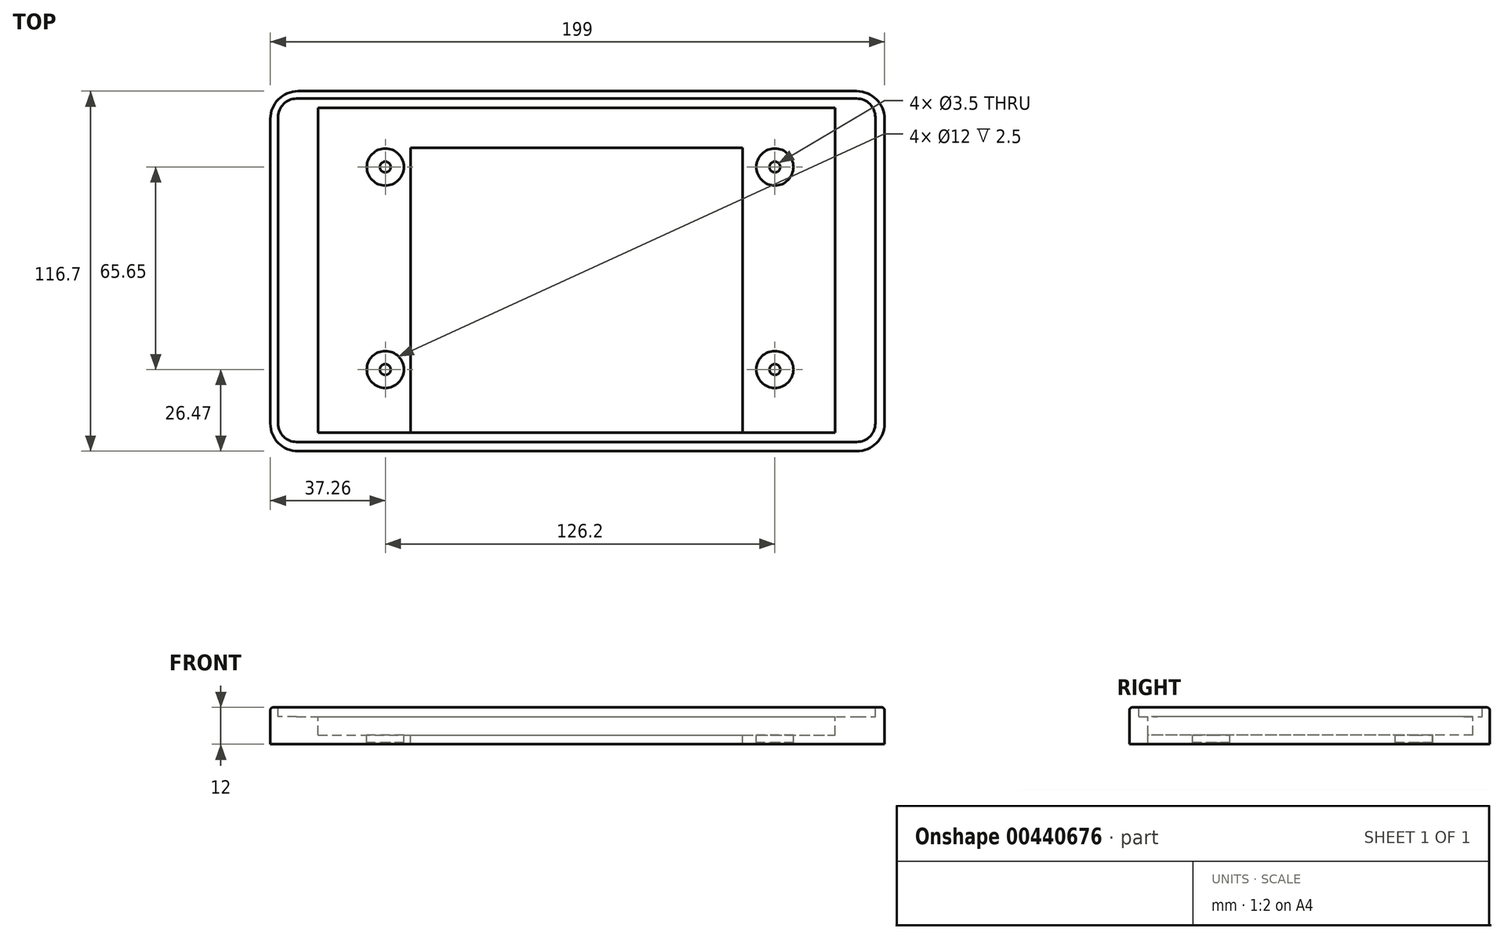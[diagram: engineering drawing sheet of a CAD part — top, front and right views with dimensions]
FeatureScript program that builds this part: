
annotation { "Feature Type Name" : "Feature", "Feature Type Description" : "" }
export const myFeature = defineFeature(function(context is Context, id is Id, definition is map)
    precondition{}
    {
        {
            var Q0;
            Q0=qCreatedBy(makeId("Top.planeOp"),FACE);
            var sketch = newSketch(context, id + "F0", { "sketchPlane" : qUnion([Q0])});
            skLineSegment(sketch, "E0.bottom", {"start": v(-90.25, 58.35) * mm, "end": v(90.75, 58.35) * mm});
            skLineSegment(sketch, "E0.top", {"start": v(-90.25, -58.35) * mm, "end": v(90.75, -58.35) * mm});
            skLineSegment(sketch, "E0.left", {"start": v(-99.25, 49.35) * mm, "end": v(-99.25, -49.35) * mm});
            skLineSegment(sketch, "E0.right", {"start": v(99.75, 49.35) * mm, "end": v(99.75, -49.35) * mm});
            skPoint(sketch, "E1.visualSharp", {"position": v(-99.25, 58.35) * mm});
            skArc(sketch, "E1.filletArc", {"start": v(-90.25, 58.35) * mm, "mid": v(-96.61, 55.71) * mm, "end": v(-99.25, 49.35) * mm});
            skPoint(sketch, "E2.visualSharp", {"position": v(-99.25, -58.35) * mm});
            skArc(sketch, "E2.filletArc", {"start": v(-99.25, -49.35) * mm, "mid": v(-96.61, -55.71) * mm, "end": v(-90.25, -58.35) * mm});
            skPoint(sketch, "E3.visualSharp", {"position": v(99.75, -58.35) * mm});
            skArc(sketch, "E3.filletArc", {"start": v(90.75, -58.35) * mm, "mid": v(97.11, -55.71) * mm, "end": v(99.75, -49.35) * mm});
            skPoint(sketch, "E4.visualSharp", {"position": v(99.75, 58.35) * mm});
            skArc(sketch, "E4.filletArc", {"start": v(99.75, 49.35) * mm, "mid": v(97.11, 55.71) * mm, "end": v(90.75, 58.35) * mm});
            skSolve(sketch);
        }
        {
            var Q0;
            Q0=makeQuery(id+"F0.imprint","IMPRINT",FACE,{"disambiguationData":[TD([[makeQuery(id+"F0.imprint","IMPRINT",EDGE,{"derivedFrom":sQuery(id+"F0.wireOp",EDGE,"E0.bottom")}),-1.0]])]});
            extrude(context, id + "F1", {"entities" : qUnion([Q0]), "depth" : 12 * mm});
        }
        {
            var Q0;
            Q0=makeQuery(id+"F1.opExtrude","CAP_FACE",FACE,{"disambiguationData":[OSD([sQuery(id+"F0.wireOp",EDGE,"E0.bottom"),sQuery(id+"F0.wireOp",EDGE,"E0.top"),sQuery(id+"F0.wireOp",EDGE,"E0.left"),sQuery(id+"F0.wireOp",EDGE,"E0.right"),sQuery(id+"F0.wireOp",EDGE,"E1.filletArc"),sQuery(id+"F0.wireOp",EDGE,"E2.filletArc"),sQuery(id+"F0.wireOp",EDGE,"E3.filletArc"),sQuery(id+"F0.wireOp",EDGE,"E4.filletArc")])],"isStart":false});
            var sketch = newSketch(context, id + "F2", { "sketchPlane" : qUnion([Q0])});
            skCircle(sketch, "E5", {"center": v(-61.99, 33.77) * mm, "radius": 1.75 * mm});
            skCircle(sketch, "E6", {"center": v(64.21, 33.77) * mm, "radius": 1.75 * mm});
            skCircle(sketch, "E7", {"center": v(64.21, -31.88) * mm, "radius": 1.75 * mm});
            skCircle(sketch, "E8", {"center": v(-61.99, -31.88) * mm, "radius": 1.75 * mm});
            skSolve(sketch);
        }
        {
            var Q0;
            Q0 = qSketchRegion(id + "F2", true);
            extrude(context, id + "F3", {"entities" : qUnion([Q0]), "operationType" : NewBodyOperationType.REMOVE, "oppositeDirection" : true, "depth" : 25 * mm});
        }
        {
            var Q0;
            Q0=makeQuery(id+"F1.opExtrude","CAP_FACE",FACE,{"disambiguationData":[OSD([sQuery(id+"F0.wireOp",EDGE,"E0.bottom"),sQuery(id+"F0.wireOp",EDGE,"E0.top"),sQuery(id+"F0.wireOp",EDGE,"E0.left"),sQuery(id+"F0.wireOp",EDGE,"E0.right"),sQuery(id+"F0.wireOp",EDGE,"E1.filletArc"),sQuery(id+"F0.wireOp",EDGE,"E2.filletArc"),sQuery(id+"F0.wireOp",EDGE,"E3.filletArc"),sQuery(id+"F0.wireOp",EDGE,"E4.filletArc")])],"isStart":false});
            var sketch = newSketch(context, id + "F4", { "sketchPlane" : qUnion([Q0])});
            skLineSegment(sketch, "E9.bottom", {"start": v(-90.75, 55.95) * mm, "end": v(90.75, 55.95) * mm});
            skLineSegment(sketch, "E9.top", {"start": v(-90.75, -55.35) * mm, "end": v(90.75, -55.35) * mm});
            skLineSegment(sketch, "E9.left", {"start": v(-96.75, 49.95) * mm, "end": v(-96.75, -49.35) * mm});
            skLineSegment(sketch, "E9.right", {"start": v(96.75, 49.95) * mm, "end": v(96.75, -49.35) * mm});
            skPoint(sketch, "E10.visualSharp", {"position": v(-96.75, -55.35) * mm});
            skArc(sketch, "E10.filletArc", {"start": v(-96.75, -49.35) * mm, "mid": v(-95, -53.6) * mm, "end": v(-90.75, -55.35) * mm});
            skPoint(sketch, "E11.visualSharp", {"position": v(96.75, -55.35) * mm});
            skArc(sketch, "E11.filletArc", {"start": v(90.75, -55.35) * mm, "mid": v(95, -53.6) * mm, "end": v(96.75, -49.35) * mm});
            skPoint(sketch, "E12.visualSharp", {"position": v(96.75, 55.95) * mm});
            skArc(sketch, "E12.filletArc", {"start": v(96.75, 49.95) * mm, "mid": v(95, 54.2) * mm, "end": v(90.75, 55.95) * mm});
            skPoint(sketch, "E13.visualSharp", {"position": v(-96.75, 55.95) * mm});
            skArc(sketch, "E13.filletArc", {"start": v(-90.75, 55.95) * mm, "mid": v(-95, 54.2) * mm, "end": v(-96.75, 49.95) * mm});
            skSolve(sketch);
        }
        {
            var Q0;
            Q0=makeQuery(id+"F4.imprint","IMPRINT",FACE,{"disambiguationData":[TD([[makeQuery(id+"F4.imprint","IMPRINT",EDGE,{"derivedFrom":sQuery(id+"F4.wireOp",EDGE,"E9.bottom")}),-1.0]])]});
            extrude(context, id + "F5", {"entities" : qUnion([Q0]), "operationType" : NewBodyOperationType.REMOVE, "oppositeDirection" : true, "depth" : 3 * mm});
        }
        {
            var Q0;
            Q0=makeQuery(id+"F1.opExtrude","CAP_EDGE",EDGE,{"disambiguationData":[OSD([sQuery(id+"F0.wireOp",EDGE,"E0.left")])],"isStart":false});
            var Q1;
            Q1=makeQuery(id+"F5.boolean.opBoolean","COPY",EDGE,{"derivedFrom":makeQuery(id+"F5.opExtrude","CAP_EDGE",EDGE,{"disambiguationData":[OSD([sQuery(id+"F4.wireOp",EDGE,"E9.left")])],"isStart":true})});
            var Q2;
            Q2=makeQuery(id+"F1.opExtrude","CAP_EDGE",EDGE,{"disambiguationData":[OSD([sQuery(id+"F0.wireOp",EDGE,"E1.filletArc")])],"isStart":false});
            var Q3;
            Q3=makeQuery(id+"F5.boolean.opBoolean","COPY",EDGE,{"derivedFrom":makeQuery(id+"F5.opExtrude","CAP_EDGE",EDGE,{"disambiguationData":[OSD([sQuery(id+"F4.wireOp",EDGE,"E9.bottom")])],"isStart":true})});
            var Q4;
            Q4=makeQuery(id+"F1.opExtrude","CAP_EDGE",EDGE,{"disambiguationData":[OSD([sQuery(id+"F0.wireOp",EDGE,"E0.bottom")])],"isStart":false});
            var Q5;
            Q5=makeQuery(id+"F5.boolean.opBoolean","COPY",EDGE,{"derivedFrom":makeQuery(id+"F5.opExtrude","CAP_EDGE",EDGE,{"disambiguationData":[OSD([sQuery(id+"F4.wireOp",EDGE,"E12.filletArc")])],"isStart":true})});
            var Q6;
            Q6=makeQuery(id+"F1.opExtrude","CAP_EDGE",EDGE,{"disambiguationData":[OSD([sQuery(id+"F0.wireOp",EDGE,"E0.right")])],"isStart":false});
            var Q7;
            Q7=makeQuery(id+"F5.boolean.opBoolean","COPY",EDGE,{"derivedFrom":makeQuery(id+"F5.opExtrude","CAP_EDGE",EDGE,{"disambiguationData":[OSD([sQuery(id+"F4.wireOp",EDGE,"E9.right")])],"isStart":true})});
            var Q8;
            Q8=makeQuery(id+"F1.opExtrude","CAP_EDGE",EDGE,{"disambiguationData":[OSD([sQuery(id+"F0.wireOp",EDGE,"E3.filletArc")])],"isStart":false});
            var Q9;
            Q9=makeQuery(id+"F5.boolean.opBoolean","COPY",EDGE,{"derivedFrom":makeQuery(id+"F5.opExtrude","CAP_EDGE",EDGE,{"disambiguationData":[OSD([sQuery(id+"F4.wireOp",EDGE,"E11.filletArc")])],"isStart":true})});
            var Q10;
            Q10=makeQuery(id+"F1.opExtrude","CAP_EDGE",EDGE,{"disambiguationData":[OSD([sQuery(id+"F0.wireOp",EDGE,"E0.top")])],"isStart":false});
            var Q11;
            Q11=makeQuery(id+"F5.boolean.opBoolean","COPY",EDGE,{"derivedFrom":makeQuery(id+"F5.opExtrude","CAP_EDGE",EDGE,{"disambiguationData":[OSD([sQuery(id+"F4.wireOp",EDGE,"E9.top")])],"isStart":true})});
            var Q12;
            Q12=makeQuery(id+"F5.boolean.opBoolean","COPY",EDGE,{"derivedFrom":makeQuery(id+"F5.opExtrude","CAP_EDGE",EDGE,{"disambiguationData":[OSD([sQuery(id+"F4.wireOp",EDGE,"E10.filletArc")])],"isStart":true})});
            var Q13;
            Q13=makeQuery(id+"F1.opExtrude","CAP_EDGE",EDGE,{"disambiguationData":[OSD([sQuery(id+"F0.wireOp",EDGE,"E2.filletArc")])],"isStart":false});
            var Q14;
            Q14=makeQuery(id+"F1.opExtrude","CAP_EDGE",EDGE,{"disambiguationData":[OSD([sQuery(id+"F0.wireOp",EDGE,"E4.filletArc")])],"isStart":false});
            var Q15;
            Q15=makeQuery(id+"F5.boolean.opBoolean","COPY",EDGE,{"derivedFrom":makeQuery(id+"F5.opExtrude","CAP_EDGE",EDGE,{"disambiguationData":[OSD([sQuery(id+"F4.wireOp",EDGE,"E13.filletArc")])],"isStart":true})});
            fillet(context, id + "F6", {"entities" : qUnion([Q0, Q1, Q2, Q3, Q4, Q5, Q6, Q7, Q8, Q9, Q10, Q11, Q12, Q13, Q14, Q15]), "radius" : 1 * mm, "tangentPropagation" : true, "allowEdgeOverflow" : false});
        }
        {
            var Q0;
            Q0=makeQuery(id+"F5.boolean.opBoolean","COPY",FACE,{"derivedFrom":makeQuery(id+"F5.opExtrude","CAP_FACE",FACE,{"disambiguationData":[OSD([sQuery(id+"F2.wireOp",EDGE,"E5"),sQuery(id+"F2.wireOp",EDGE,"E6"),sQuery(id+"F2.wireOp",EDGE,"E7"),sQuery(id+"F2.wireOp",EDGE,"E8"),sQuery(id+"F4.wireOp",EDGE,"E9.bottom"),sQuery(id+"F4.wireOp",EDGE,"E9.top"),sQuery(id+"F4.wireOp",EDGE,"E9.left"),sQuery(id+"F4.wireOp",EDGE,"E9.right"),sQuery(id+"F4.wireOp",EDGE,"E10.filletArc"),sQuery(id+"F4.wireOp",EDGE,"E11.filletArc"),sQuery(id+"F4.wireOp",EDGE,"E12.filletArc"),sQuery(id+"F4.wireOp",EDGE,"E13.filletArc")])],"isStart":false})});
            var sketch = newSketch(context, id + "F7", { "sketchPlane" : qUnion([Q0])});
            skLineSegment(sketch, "E14.bottom", {"start": v(-83.75, 52.95) * mm, "end": v(83.75, 52.95) * mm});
            skLineSegment(sketch, "E14.top", {"start": v(-83.75, -52.35) * mm, "end": v(83.75, -52.35) * mm});
            skLineSegment(sketch, "E14.left", {"start": v(-83.75, 52.95) * mm, "end": v(-83.75, -52.35) * mm});
            skLineSegment(sketch, "E14.right", {"start": v(83.75, 52.95) * mm, "end": v(83.75, -52.35) * mm});
            skSolve(sketch);
        }
        {
            var Q0;
            Q0=makeQuery(id+"F7.imprint","IMPRINT",FACE,{"disambiguationData":[TD([[makeQuery(id+"F7.imprint","IMPRINT",EDGE,{"derivedFrom":sQuery(id+"F7.wireOp",EDGE,"E14.bottom")}),-1.0]])]});
            extrude(context, id + "F8", {"entities" : qUnion([Q0]), "operationType" : NewBodyOperationType.REMOVE, "oppositeDirection" : true, "depth" : 6 * mm});
        }
        {
            var Q0;
            Q0=makeQuery(id+"F8.boolean.opBoolean","COPY",FACE,{"derivedFrom":makeQuery(id+"F8.opExtrude","CAP_FACE",FACE,{"disambiguationData":[OSD([sQuery(id+"F2.wireOp",EDGE,"E5"),sQuery(id+"F2.wireOp",EDGE,"E6"),sQuery(id+"F2.wireOp",EDGE,"E7"),sQuery(id+"F2.wireOp",EDGE,"E8"),sQuery(id+"F7.wireOp",EDGE,"E14.bottom"),sQuery(id+"F7.wireOp",EDGE,"E14.top"),sQuery(id+"F7.wireOp",EDGE,"E14.left"),sQuery(id+"F7.wireOp",EDGE,"E14.right")])],"isStart":false})});
            var sketch = newSketch(context, id + "F9", { "sketchPlane" : qUnion([Q0])});
            skLineSegment(sketch, "E15.bottom", {"start": v(-53.75, 39.95) * mm, "end": v(53.75, 39.95) * mm});
            skLineSegment(sketch, "E15.top", {"start": v(-53.75, -52.35) * mm, "end": v(53.75, -52.35) * mm});
            skLineSegment(sketch, "E15.left", {"start": v(-53.75, 39.95) * mm, "end": v(-53.75, -52.35) * mm});
            skLineSegment(sketch, "E15.right", {"start": v(53.75, 39.95) * mm, "end": v(53.75, -52.35) * mm});
            skSolve(sketch);
        }
        {
            var Q0;
            Q0=makeQuery(id+"F9.imprint","IMPRINT",FACE,{"disambiguationData":[TD([[makeQuery(id+"F9.imprint","IMPRINT",EDGE,{"derivedFrom":sQuery(id+"F9.wireOp",EDGE,"E15.bottom")}),-1.0]])]});
            extrude(context, id + "F10", {"entities" : qUnion([Q0]), "operationType" : NewBodyOperationType.REMOVE, "oppositeDirection" : true, "depth" : 6 * mm});
        }
        {
            var Q0;
            Q0=makeQuery(id+"F8.boolean.opBoolean","COPY",FACE,{"derivedFrom":makeQuery(id+"F8.opExtrude","CAP_FACE",FACE,{"disambiguationData":[OSD([sQuery(id+"F2.wireOp",EDGE,"E5"),sQuery(id+"F2.wireOp",EDGE,"E6"),sQuery(id+"F2.wireOp",EDGE,"E7"),sQuery(id+"F2.wireOp",EDGE,"E8"),sQuery(id+"F7.wireOp",EDGE,"E14.bottom"),sQuery(id+"F7.wireOp",EDGE,"E14.top"),sQuery(id+"F7.wireOp",EDGE,"E14.left"),sQuery(id+"F7.wireOp",EDGE,"E14.right")])],"isStart":false})});
            var sketch = newSketch(context, id + "F11", { "sketchPlane" : qUnion([Q0])});
            skCircle(sketch, "E16", {"center": v(-61.99, 33.77) * mm, "radius": 6 * mm});
            skCircle(sketch, "E17", {"center": v(-61.99, -31.88) * mm, "radius": 6 * mm});
            skCircle(sketch, "E18", {"center": v(64.21, 33.77) * mm, "radius": 6 * mm});
            skCircle(sketch, "E19", {"center": v(64.21, -31.88) * mm, "radius": 6 * mm});
            skSolve(sketch);
        }
        {
            var Q0;
            Q0=makeQuery(id+"F11.imprint","IMPRINT",FACE,{"disambiguationData":[TD([[makeQuery(id+"F11.imprint","IMPRINT",EDGE,{"derivedFrom":sQuery(id+"F11.wireOp",EDGE,"E16")}),1.0]])]});
            var Q1;
            Q1=makeQuery(id+"F11.imprint","IMPRINT",FACE,{"disambiguationData":[TD([[makeQuery(id+"F11.imprint","IMPRINT",EDGE,{"derivedFrom":sQuery(id+"F11.wireOp",EDGE,"E17")}),1.0]])]});
            var Q2;
            Q2=makeQuery(id+"F11.imprint","IMPRINT",FACE,{"disambiguationData":[TD([[makeQuery(id+"F11.imprint","IMPRINT",EDGE,{"derivedFrom":sQuery(id+"F11.wireOp",EDGE,"E18")}),1.0]])]});
            var Q3;
            Q3=makeQuery(id+"F11.imprint","IMPRINT",FACE,{"disambiguationData":[TD([[makeQuery(id+"F11.imprint","IMPRINT",EDGE,{"derivedFrom":sQuery(id+"F11.wireOp",EDGE,"E19")}),1.0]])]});
            extrude(context, id + "F12", {"entities" : qUnion([Q0, Q1, Q2, Q3]), "operationType" : NewBodyOperationType.REMOVE, "oppositeDirection" : true, "depth" : 2.5 * mm});
        }
    });
